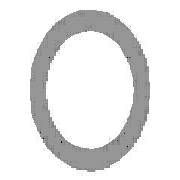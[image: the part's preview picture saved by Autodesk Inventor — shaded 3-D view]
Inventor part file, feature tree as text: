
AUTODESK INVENTOR PART (.ipt)
format: ipt  version: 2024.3 (Build 283343000, 343)  size: 120,320 bytes
history: native  units: mm (DEFAULTED — no unit token found)
features: other x4, sketch x1, plane x1
ambient origin geometry x8: Origin, YZ Plane, XZ Plane, XY Plane, X Axis, Y Axis, Z Axis, Center Point
bodies: Solid1 (feature_tree), Body (feature_tree)
feature tree (6):
  parser-record x1  (decoder bookkeeping rows leaked as tree rows — omitted from the tree; the rows remain in map.json)
  other  "Driven Length"
  other  "Start Plane"
  other  "End Plane"
  sketch  "Sketch3"  dims[d0=42.4mm d1=2.0mm d2=800.0mm d3=0.0mm d4=-0.0mm d5=800.0mm d6=90.0deg d7=800.0mm]
  plane  "Work Plane3"
